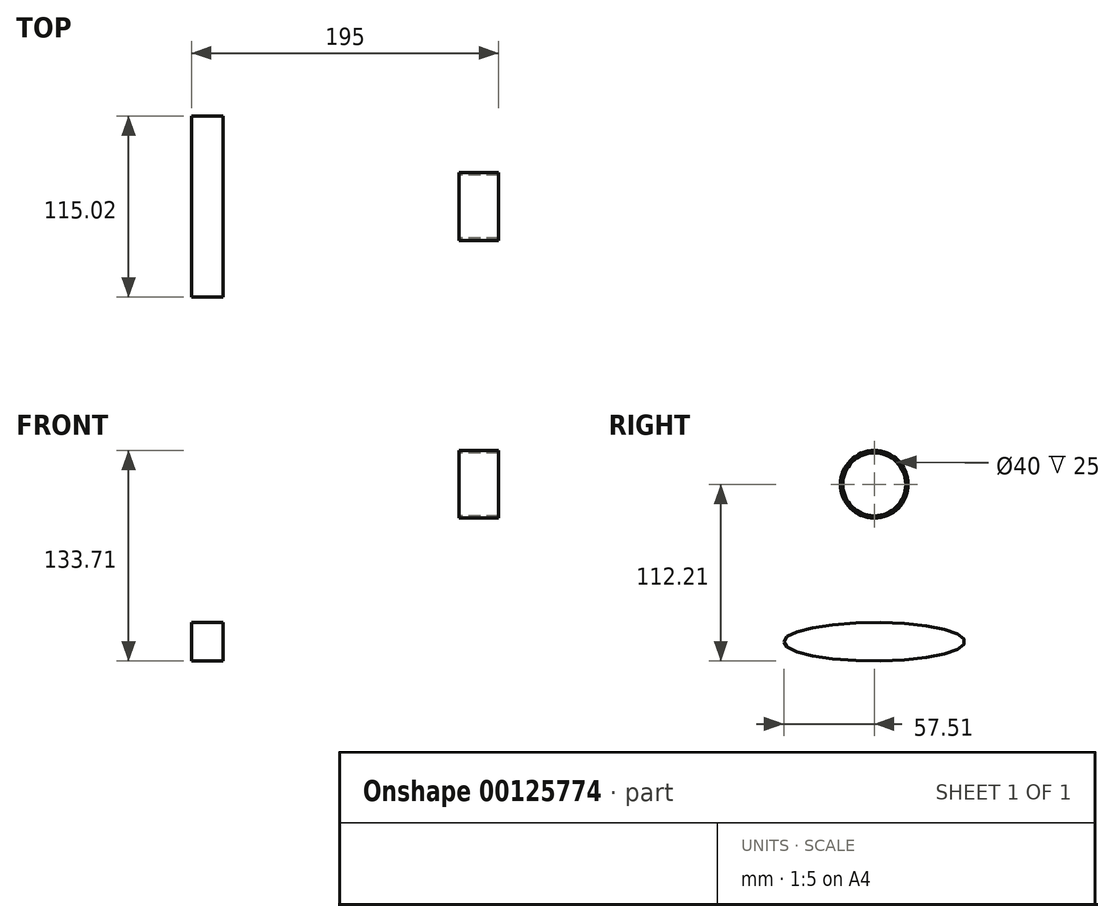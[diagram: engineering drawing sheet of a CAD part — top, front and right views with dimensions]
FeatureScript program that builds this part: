
annotation { "Feature Type Name" : "Feature", "Feature Type Description" : "" }
export const myFeature = defineFeature(function(context is Context, id is Id, definition is map)
    precondition{}
    {
        {
            var Q0;
            Q0=qCreatedBy(makeId("Right.planeOp"),FACE);
            var sketch = newSketch(context, id + "F0", { "sketchPlane" : qUnion([Q0])});
            skCircle(sketch, "E0", {"center": v(0, 0) * mm, "radius": 20 * mm});
            skCircle(sketch, "E1", {"center": v(0, 0) * mm, "radius": 21.5 * mm});
            skSolve(sketch);
        }
        {
            var Q0;
            Q0=qCreatedBy(makeId("Right.planeOp"),FACE);
            cPlane(context, id + "F1", {"entities" : qUnion([Q0]), "cplaneType" : CPlaneType.OFFSET, "offset" : 150 * mm, "oppositeDirection" : true, "width" : 150 * mm, "height" : 150 * mm});
        }
        {
            var Q0;
            Q0=makeQuery(id+"F0.imprint","IMPRINT",FACE,{"disambiguationData":[TD([[makeQuery(id+"F0.imprint","IMPRINT",EDGE,{"derivedFrom":sQuery(id+"F0.wireOp",EDGE,"E0")}),-1.0]])]});
            extrude(context, id + "F2", {"entities" : qUnion([Q0]), "depth" : 25 * mm});
        }
        {
            var Q0;
            Q0=qCreatedBy(id+"F1.planeOp",FACE);
            var sketch = newSketch(context, id + "F3", { "sketchPlane" : qUnion([Q0])});
            skEllipse(sketch, "E2", {"center": v(0, -100) * mm, "majorRadius": 57.5 * mm, "minorRadius": 12.2 * mm, "majorAxis": v(-1, 0)});
            skFitSpline(sketch, "E3.0", {"points": [v(-58.93, -99.04) * mm, v(-59.05, -100) * mm, v(-58.93, -100.96) * mm, v(-58.61, -101.85) * mm, v(-58.13, -102.68) * mm, v(-57.3, -103.68) * mm, v(-55.96, -104.8) * mm, v(-53.9, -106.02) * mm, v(-51.36, -107.16) * mm, v(-48.38, -108.22) * mm, v(-45.5, -109.04) * mm, v(-43, -109.66) * mm, v(-41, -110.1) * mm, v(-38.9, -110.53) * mm, v(-36, -111.06) * mm, v(-32.16, -111.66) * mm, v(-27.29, -112.28) * mm, v(-22.17, -112.8) * mm, v(-16.85, -113.2) * mm, v(-11.36, -113.5) * mm, v(-6.67, -113.64) * mm, v(-2.87, -113.7) * mm, v(0, -113.71) * mm, v(2.87, -113.7) * mm, v(6.67, -113.64) * mm, v(11.36, -113.5) * mm, v(16.85, -113.2) * mm, v(22.17, -112.8) * mm, v(27.29, -112.28) * mm, v(32.16, -111.66) * mm, v(36, -111.06) * mm, v(38.9, -110.53) * mm, v(41, -110.1) * mm, v(43, -109.66) * mm, v(45.5, -109.04) * mm, v(48.38, -108.22) * mm, v(51.36, -107.16) * mm, v(53.9, -106.02) * mm, v(55.96, -104.8) * mm, v(57.3, -103.68) * mm, v(58.13, -102.68) * mm, v(58.61, -101.85) * mm, v(58.93, -100.96) * mm, v(59.05, -100) * mm, v(58.93, -99.04) * mm, v(58.61, -98.15) * mm, v(58.13, -97.32) * mm, v(57.3, -96.32) * mm, v(55.96, -95.2) * mm, v(53.9, -93.98) * mm, v(51.36, -92.84) * mm, v(48.38, -91.78) * mm, v(45.5, -90.96) * mm, v(43, -90.34) * mm, v(41, -89.9) * mm, v(38.9, -89.47) * mm, v(36, -88.94) * mm, v(32.16, -88.34) * mm, v(27.29, -87.72) * mm, v(22.17, -87.2) * mm, v(16.85, -86.8) * mm, v(11.36, -86.5) * mm, v(6.67, -86.36) * mm, v(2.87, -86.3) * mm, v(0, -86.29) * mm, v(-2.87, -86.3) * mm, v(-6.67, -86.36) * mm, v(-11.36, -86.5) * mm, v(-16.85, -86.8) * mm, v(-22.17, -87.2) * mm, v(-27.29, -87.72) * mm, v(-32.16, -88.34) * mm, v(-36, -88.94) * mm, v(-38.9, -89.47) * mm, v(-41, -89.9) * mm, v(-43, -90.34) * mm, v(-45.5, -90.96) * mm, v(-48.38, -91.78) * mm, v(-51.36, -92.84) * mm, v(-53.9, -93.98) * mm, v(-55.96, -95.2) * mm, v(-57.3, -96.32) * mm, v(-58.13, -97.32) * mm, v(-58.61, -98.15) * mm, v(-58.93, -99.04) * mm, v(-59.05, -100) * mm, v(-58.93, -100.96) * mm, v(-58.93, -99.04) * mm]});
            skSolve(sketch);
        }
        {
            var Q0;
            Q0 = qSketchRegion(id + "F3", true);
            extrude(context, id + "F4", {"entities" : qUnion([Q0]), "oppositeDirection" : true, "depth" : 20 * mm});
        }
    });
